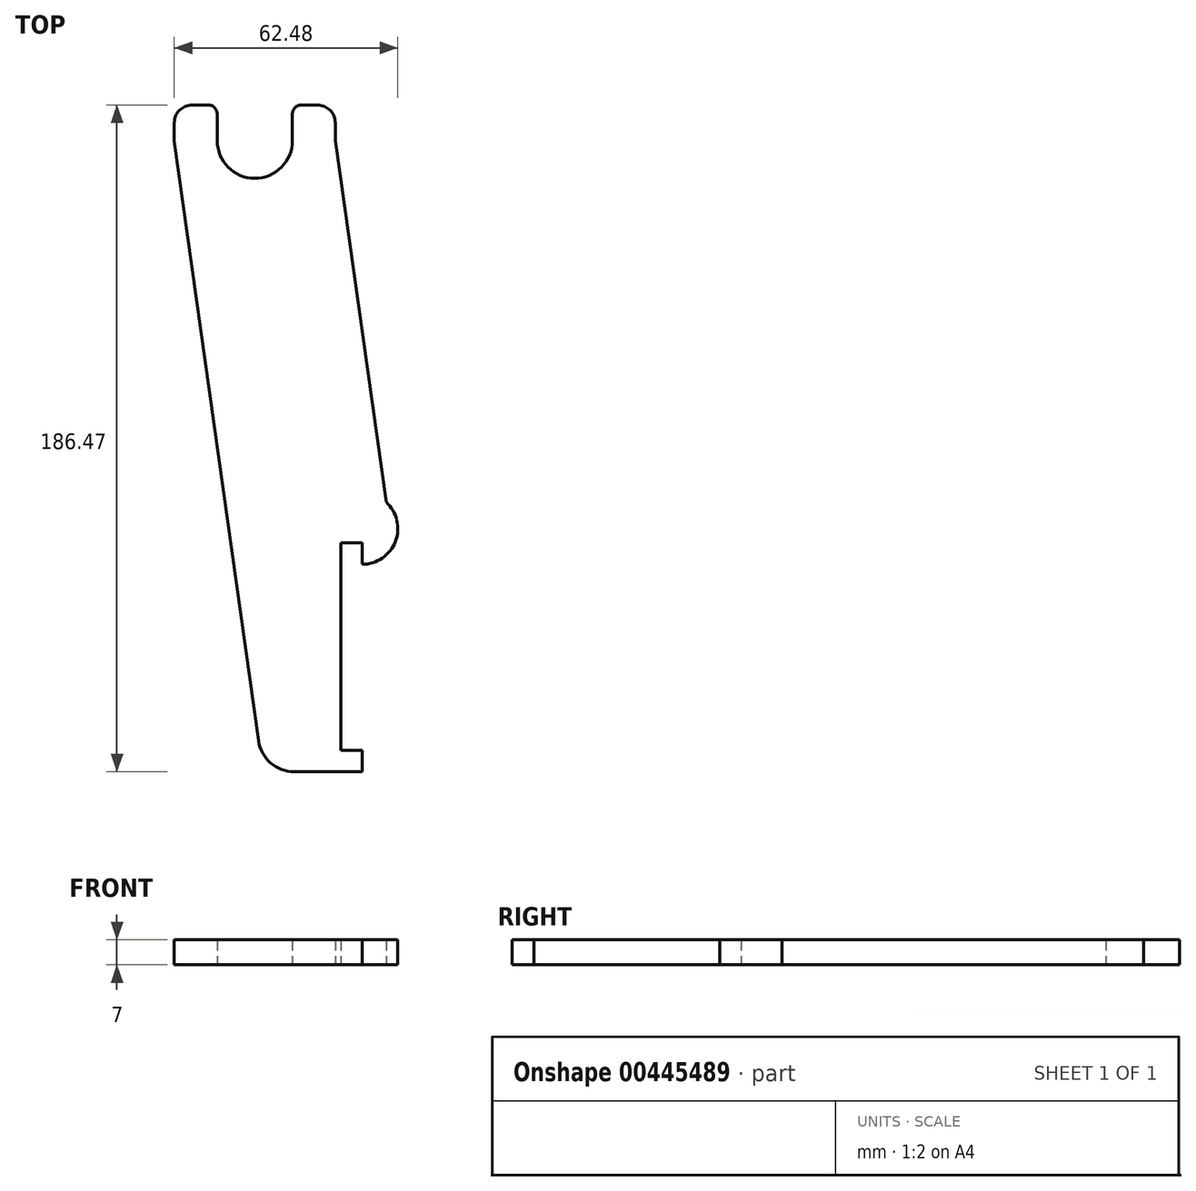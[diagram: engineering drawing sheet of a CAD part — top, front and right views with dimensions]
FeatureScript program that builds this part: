
annotation { "Feature Type Name" : "Feature", "Feature Type Description" : "" }
export const myFeature = defineFeature(function(context is Context, id is Id, definition is map)
    precondition{}
    {
        {
            var Q0;
            Q0=qCreatedBy(makeId("Top.planeOp"),FACE);
            var sketch = newSketch(context, id + "F0", { "sketchPlane" : qUnion([Q0])});
            skLineSegment(sketch, "E0", {"start": v(9.94, -0.86) * mm, "end": v(9.94, 5.14) * mm});
            skLineSegment(sketch, "E1", {"start": v(9.94, 5.14) * mm, "end": v(3.94, 5.14) * mm});
            skLineSegment(sketch, "E2", {"start": v(3.94, 5.14) * mm, "end": v(3.94, -52.86) * mm});
            skLineSegment(sketch, "E3", {"start": v(3.94, -52.86) * mm, "end": v(9.94, -52.86) * mm});
            skLineSegment(sketch, "E4", {"start": v(9.94, -52.86) * mm, "end": v(9.94, -58.86) * mm});
            skLineSegment(sketch, "E5", {"start": v(9.94, -58.86) * mm, "end": v(-9.07, -58.86) * mm});
            skLineSegment(sketch, "E6", {"start": v(-18.98, -50.25) * mm, "end": v(-42.56, 117.6) * mm});
            skLineSegment(sketch, "E7", {"start": v(9.94, -0.86) * mm, "end": v(9.94, -0.86) * mm});
            skArc(sketch, "E8", {"start": v(-30.56, 117.6) * mm, "mid": v(-20.06, 107.1) * mm, "end": v(-9.56, 117.6) * mm});
            skLineSegment(sketch, "E9", {"start": v(-42.56, 117.6) * mm, "end": v(-42.56, 122.6) * mm});
            skLineSegment(sketch, "E10", {"start": v(-37.56, 127.6) * mm, "end": v(-33.06, 127.6) * mm});
            skLineSegment(sketch, "E11", {"start": v(-30.56, 125.1) * mm, "end": v(-30.56, 117.6) * mm});
            skLineSegment(sketch, "E12", {"start": v(2.44, 117.6) * mm, "end": v(2.44, 122.6) * mm});
            skLineSegment(sketch, "E13", {"start": v(-2.56, 127.6) * mm, "end": v(-7.06, 127.6) * mm});
            skLineSegment(sketch, "E14", {"start": v(-9.56, 125.1) * mm, "end": v(-9.56, 117.6) * mm});
            skLineSegment(sketch, "E15", {"start": v(16.64, 16.54) * mm, "end": v(2.44, 117.6) * mm});
            skPoint(sketch, "E16.visualSharp", {"position": v(-17.77, -58.86) * mm});
            skArc(sketch, "E16.filletArc", {"start": v(-18.98, -50.25) * mm, "mid": v(-15.63, -56.4) * mm, "end": v(-9.07, -58.86) * mm});
            skArc(sketch, "E17", {"start": v(9.94, -0.86) * mm, "mid": v(19.25, 5.55) * mm, "end": v(16.64, 16.54) * mm});
            skPoint(sketch, "E18.visualSharp", {"position": v(-42.56, 127.6) * mm});
            skArc(sketch, "E18.filletArc", {"start": v(-37.56, 127.6) * mm, "mid": v(-41.1, 126.14) * mm, "end": v(-42.56, 122.6) * mm});
            skPoint(sketch, "E19.visualSharp", {"position": v(2.44, 127.6) * mm});
            skArc(sketch, "E19.filletArc", {"start": v(2.44, 122.6) * mm, "mid": v(0.98, 126.14) * mm, "end": v(-2.56, 127.6) * mm});
            skPoint(sketch, "E20.visualSharp", {"position": v(-30.56, 127.6) * mm});
            skArc(sketch, "E20.filletArc", {"start": v(-30.56, 125.1) * mm, "mid": v(-31.3, 126.88) * mm, "end": v(-33.06, 127.6) * mm});
            skPoint(sketch, "E21.visualSharp", {"position": v(-9.56, 127.6) * mm});
            skArc(sketch, "E21.filletArc", {"start": v(-7.06, 127.6) * mm, "mid": v(-8.83, 126.88) * mm, "end": v(-9.56, 125.1) * mm});
            skSolve(sketch);
        }
        {
            var Q0;
            Q0=makeQuery(id+"F0.imprint","IMPRINT",FACE,{"disambiguationData":[TD([[makeQuery(id+"F0.imprint","IMPRINT",EDGE,{"derivedFrom":sQuery(id+"F0.wireOp",EDGE,"E0")}),-1.0]])]});
            extrude(context, id + "F1", {"entities" : qUnion([Q0]), "depth" : 7 * mm});
        }
    });
